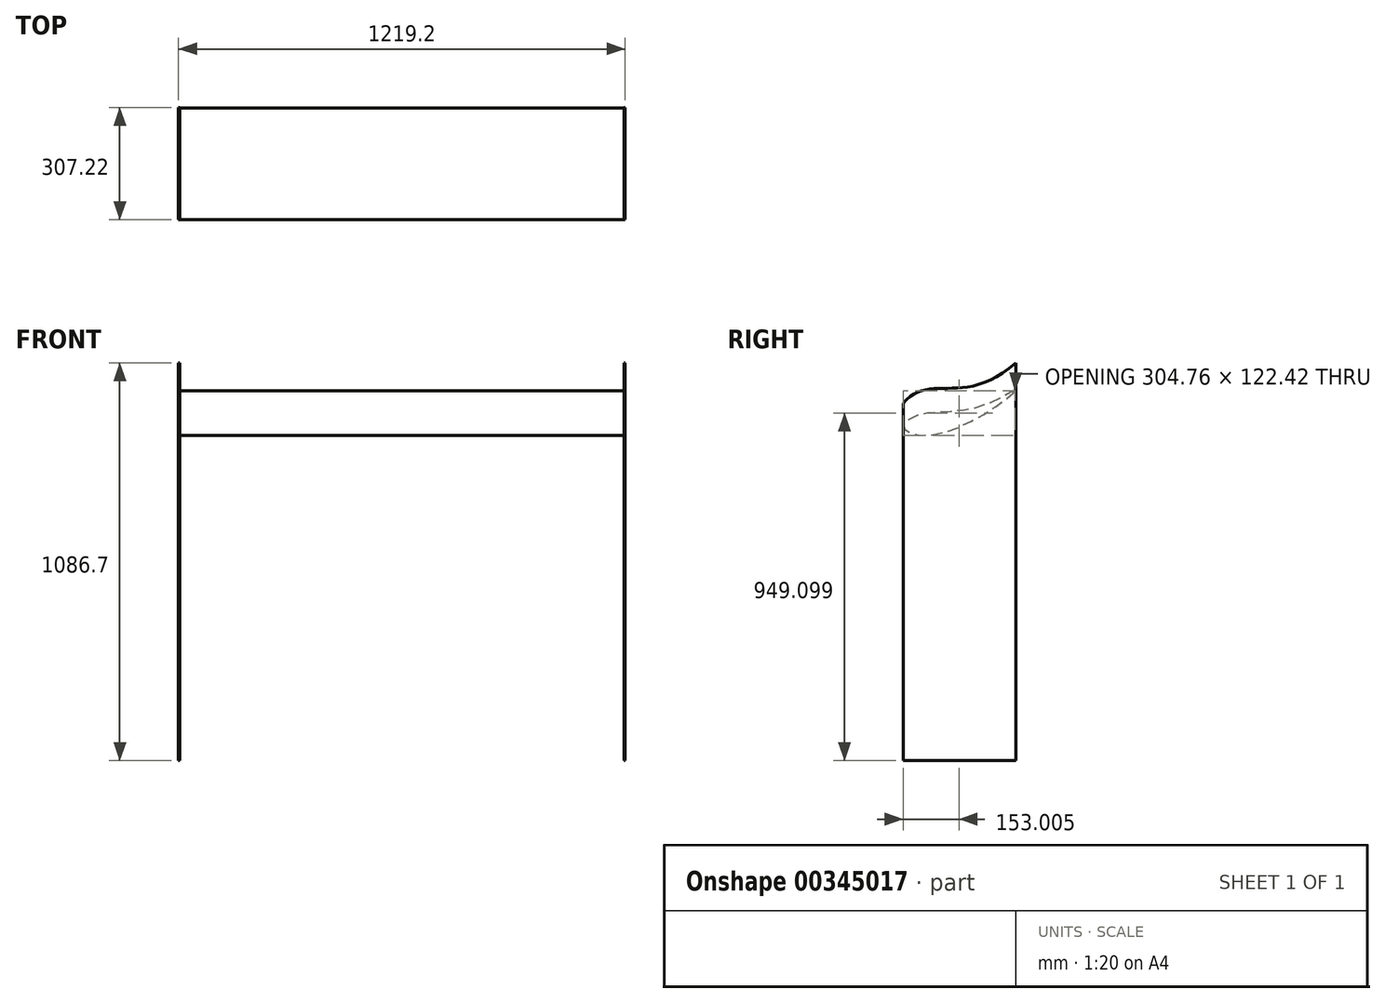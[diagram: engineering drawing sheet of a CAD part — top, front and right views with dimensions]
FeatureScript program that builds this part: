
annotation { "Feature Type Name" : "Feature", "Feature Type Description" : "" }
export const myFeature = defineFeature(function(context is Context, id is Id, definition is map)
    precondition{}
    {
        {
            var Q0;
            Q0=qCreatedBy(makeId("Right.planeOp"),FACE);
            var sketch = newSketch(context, id + "F0", { "sketchPlane" : qUnion([Q0])});
            skFitSpline(sketch, "E0", {"points": [v(43.03, 34.75) * mm, v(-59.13, -11.1) * mm, v(-212.23, -29.86) * mm, v(-261.77, -62.88) * mm, v(-206.98, -87.65) * mm, v(-23.1, -17.85) * mm, v(43.03, 34.75) * mm]});
            skLineSegment(sketch, "E1", {"start": v(43.03, 34.75) * mm, "end": v(43.03, 111.18) * mm});
            skSolve(sketch);
        }
        {
            var Q0;
            Q0=qCreatedBy(makeId("Right.planeOp"),FACE);
            var sketch = newSketch(context, id + "F1", { "sketchPlane" : qUnion([Q0])});
            skFitSpline(sketch, "E2", {"points": [v(-262.35, 0) * mm, v(44.87, 111.14) * mm], "startDerivative": vector(215.23, 265.33) * mm, "endDerivative": vector(423.55, 379.36) * mm});
            skLineSegment(sketch, "E3", {"start": v(-262.35, 0) * mm, "end": v(-262.35, -61.16) * mm});
            skLineSegment(sketch, "E4", {"start": v(-262.35, -61.16) * mm, "end": v(-262.35, -975.56) * mm});
            skLineSegment(sketch, "E5", {"start": v(-262.35, -975.56) * mm, "end": v(44.87, -975.56) * mm});
            skLineSegment(sketch, "E6", {"start": v(44.87, 111.14) * mm, "end": v(44.87, -975.56) * mm});
            skSolve(sketch);
        }
        {
            var Q0;
            Q0 = qSketchRegion(id + "F0", true);
            extrude(context, id + "F2", {"entities" : qUnion([Q0]), "depth" : 609.6 * mm});
        }
        {
            var Q0;
            Q0 = qSketchRegion(id + "F1", true);
            extrude(context, id + "F3", {"entities" : qUnion([Q0]), "operationType" : NewBodyOperationType.ADD, "depth" : 3.17 * mm});
        }
        {
            var Q0;
            Q0=makeQuery(id+"F2.opExtrude","SWEPT_BODY",BODY,{"disambiguationData":[OSD([sQuery(id+"F0.wireOp",EDGE,"E0")])]});
            var Q1;
            Q1=makeQuery(id+"F2.opExtrude","CAP_FACE",FACE,{"disambiguationData":[OSD([sQuery(id+"F0.wireOp",EDGE,"E0")])],"isStart":false});
            mirror(context, id + "F4", {"operationType" : NewBodyOperationType.ADD, "entities" : qUnion([Q0]), "mirrorPlane" : qUnion([Q1])});
        }
    });
